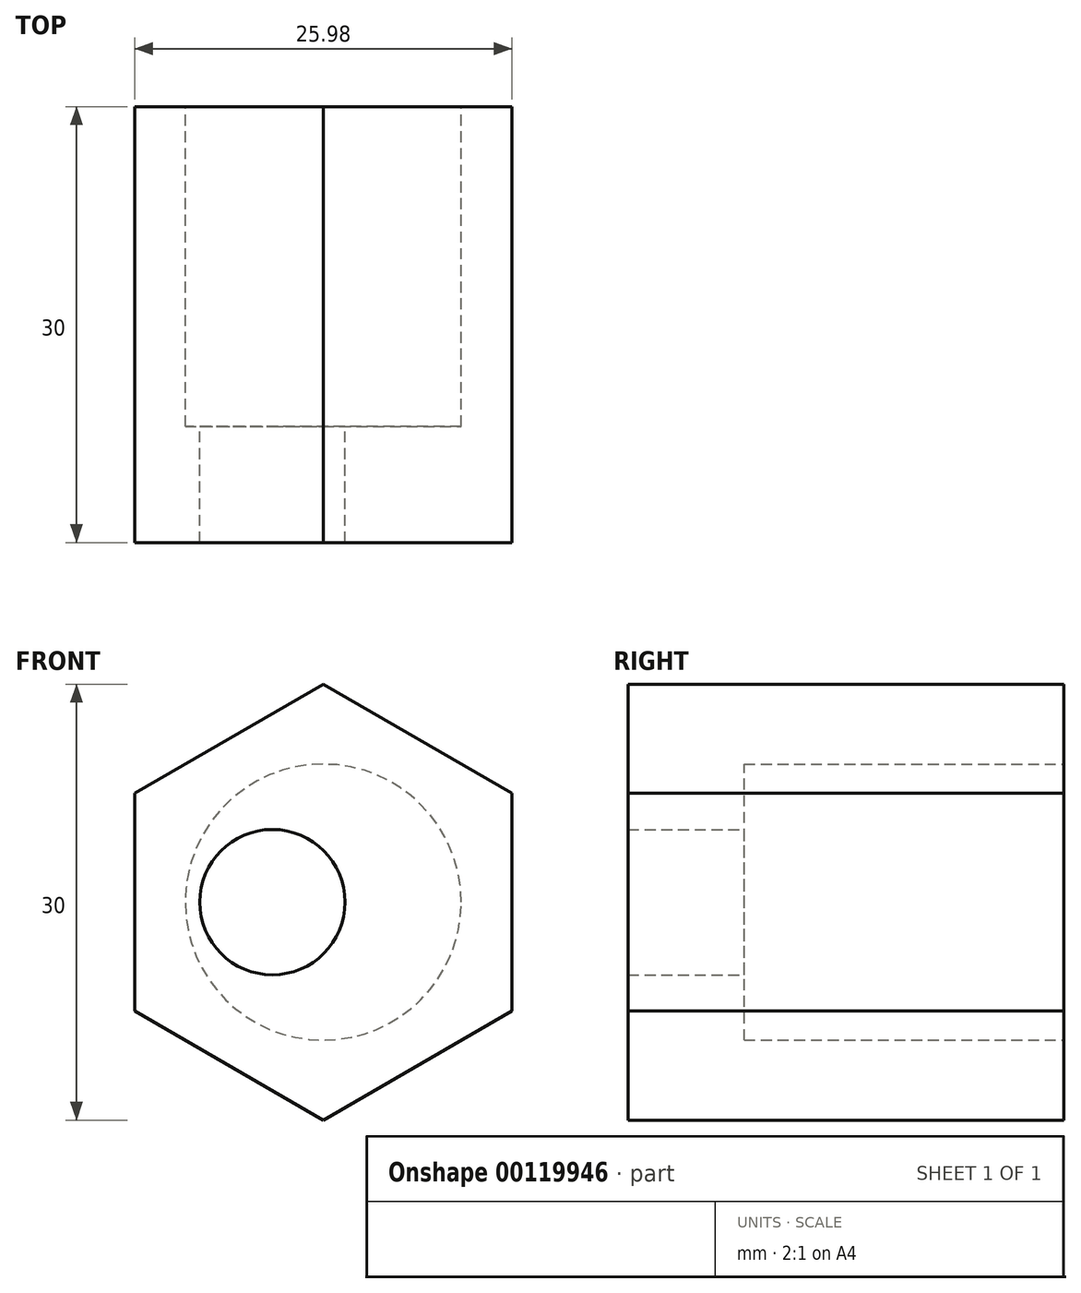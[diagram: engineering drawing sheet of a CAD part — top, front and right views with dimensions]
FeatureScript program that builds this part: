
annotation { "Feature Type Name" : "Feature", "Feature Type Description" : "" }
export const myFeature = defineFeature(function(context is Context, id is Id, definition is map)
    precondition{}
    {
        {
            var Q0;
            Q0=qCreatedBy(makeId("Front.planeOp"),FACE);
            var sketch = newSketch(context, id + "F0", { "sketchPlane" : qUnion([Q0])});
            skCircle(sketch, "E0", {"center": v(0, 0) * mm, "radius": 9.5 * mm});
            skLineSegment(sketch, "E1", {"start": v(-9.5, 0) * mm, "end": v(-8.5, 0) * mm});
            skLineSegment(sketch, "E2", {"start": v(0, 0) * mm, "end": v(-17.8, 0) * mm, "construction": true});
            skLineSegment(sketch, "E3", {"start": v(-17.8, 0) * mm, "end": v(16.16, 0) * mm, "construction": true});
            skCircle(sketch, "E4", {"center": v(-3.5, 0) * mm, "radius": 5 * mm});
            skCircle(sketch, "E5.cCircle", {"center": v(0, 0) * mm, "radius": 15 * mm, "construction": true});
            skLineSegment(sketch, "E5.0", {"start": v(-13, 7.5) * mm, "end": v(0, 15) * mm});
            skLineSegment(sketch, "E5.1", {"start": v(0, 15) * mm, "end": v(13, 7.5) * mm});
            skLineSegment(sketch, "E5.2", {"start": v(13, 7.5) * mm, "end": v(13, -7.5) * mm});
            skLineSegment(sketch, "E5.3", {"start": v(13, -7.5) * mm, "end": v(0, -15) * mm});
            skLineSegment(sketch, "E5.4", {"start": v(0, -15) * mm, "end": v(-13, -7.5) * mm});
            skLineSegment(sketch, "E5.5", {"start": v(-13, -7.5) * mm, "end": v(-13, 7.5) * mm});
            skSolve(sketch);
        }
        {
            var Q0;
            Q0=makeQuery(id+"F0.imprint","IMPRINT",FACE,{"disambiguationData":[TD([[makeQuery(id+"F0.imprint","IMPRINT",EDGE,{"derivedFrom":sQuery(id+"F0.wireOp",EDGE,"E0")}),-1.0]])]});
            var Q1;
            Q1=makeQuery(id+"F0.imprint","IMPRINT",FACE,{"disambiguationData":[TD([[makeQuery(id+"F0.imprint","IMPRINT",EDGE,{"derivedFrom":sQuery(id+"F0.wireOp",EDGE,"E0")}),1.0]])]});
            extrude(context, id + "F1", {"entities" : qUnion([Q0, Q1]), "depth" : 30 * mm});
        }
        {
            var Q0;
            Q0=makeQuery(id+"F0.imprint","IMPRINT",FACE,{"disambiguationData":[TD([[makeQuery(id+"F0.imprint","IMPRINT",EDGE,{"derivedFrom":sQuery(id+"F0.wireOp",EDGE,"E0")}),1.0]])]});
            var Q1;
            Q1=makeQuery(id+"F0.imprint","IMPRINT",FACE,{"disambiguationData":[TD([[makeQuery(id+"F0.imprint","IMPRINT",EDGE,{"derivedFrom":sQuery(id+"F0.wireOp",EDGE,"E4")}),1.0]])]});
            extrude(context, id + "F2", {"entities" : qUnion([Q0, Q1]), "depth" : 22 * mm});
        }
        {
            var Q0;
            Q0=makeQuery(id+"F2.opExtrude","SWEPT_BODY",BODY,{"disambiguationData":[OSD([sQuery(id+"F0.wireOp",EDGE,"E0")])]});
            var Q1;
            Q1=makeQuery(id+"F1.opExtrude","SWEPT_BODY",BODY,{"disambiguationData":[OSD([sQuery(id+"F0.wireOp",EDGE,"E4"),sQuery(id+"F0.wireOp",EDGE,"E5.0"),sQuery(id+"F0.wireOp",EDGE,"E5.1"),sQuery(id+"F0.wireOp",EDGE,"E5.2"),sQuery(id+"F0.wireOp",EDGE,"E5.3"),sQuery(id+"F0.wireOp",EDGE,"E5.4"),sQuery(id+"F0.wireOp",EDGE,"E5.5")])]});
            booleanBodies(context, id + "F3", {"operationType" : BooleanOperationType.SUBTRACTION, "tools" : qUnion([Q0]), "targets" : qUnion([Q1])});
        }
    });
